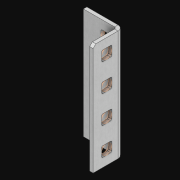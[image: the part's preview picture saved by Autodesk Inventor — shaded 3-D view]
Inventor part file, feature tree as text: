
AUTODESK INVENTOR PART (.ipt)
format: ipt  version: 2021 (Build 250183000, 183)  size: 1,036,800 bytes
history: native  units: in
note: dims shown in document units (in); Inventor stores cm internally (conversion verified against a paired STEP export)
features: extrude x10, other x8, sketch x4, pattern_linear x2, sheet_metal_op x1
ambient origin geometry x8: Origin, YZ Plane, XZ Plane, XY Plane, X Axis, Y Axis, Z Axis, Center Point
bodies: Solid1 (feature_tree)
feature tree (25):
  pattern_linear  "Rectangular Pattern1"  Spacing1=0.5in  [1 undecoded]
  pattern_linear  "Rectangular Pattern3"  Count1=4  [1 undecoded]
  extrude  "Extrusion1"  Depth=0.5in
  extrude  "Extrusion2"  Depth=0.841in
  sketch  "Sketch1"  dims[d0=0.182in]
  other  "Srf1"
  sketch  "Sketch3"  dims[d1=0.063in d2=0.0in]
  other  "Srf3"
  other  "Srf4"
  other  "Srf5"
  other  "Srf6"
  other  "Srf142"
  other  "Srf143"
  other  "Srf144"
  sketch  "Sketch4"  dims[d6=0.182in]
  sketch  "Sketch5"  dims[d7=0.063in d8=0.0in d11=0.5in d12=0.3937in d14=0.5in d18=1.5748in d20=0.5in d21=15.5in d22=0.0in d23=0.841in d24=0.0in]
  sheet_metal_op  "Fold1"
  extrude  "ExtrusionSrf1"  TaperAngle=0.0deg  [1 undecoded]
  extrude  "ExtrusionSrf3"  Depth=0.841in TaperAngle=0.0deg
  extrude  "ExtrusionSrf4"  [1 undecoded]
  extrude  "ExtrusionSrf5"  [1 undecoded]
  extrude  "ExtrusionSrf6"  [1 undecoded]
  extrude  "ExtrusionSrf142"  [1 undecoded]
  extrude  "ExtrusionSrf143"  [1 undecoded]
  extrude  "ExtrusionSrf144"  [1 undecoded]
note: 9 required parameter values undecoded (feature->parameter linkage not recoverable at this tier; creation-order binding heuristic only, values carry confidence <= 0.55)
